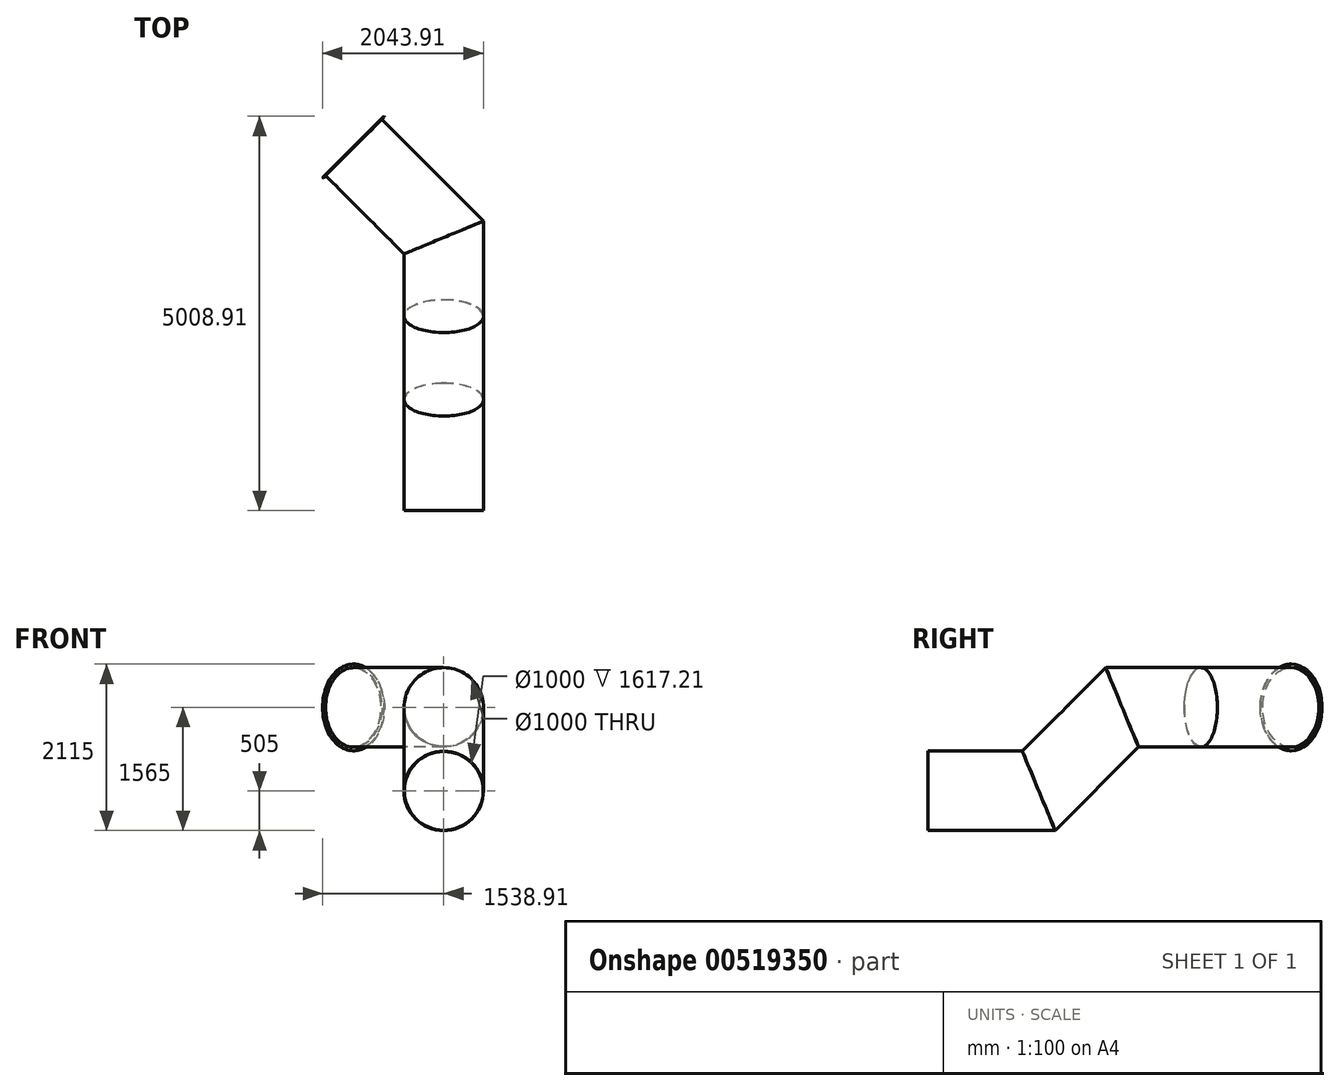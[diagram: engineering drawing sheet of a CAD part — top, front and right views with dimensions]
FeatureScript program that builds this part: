
annotation { "Feature Type Name" : "Feature", "Feature Type Description" : "" }
export const myFeature = defineFeature(function(context is Context, id is Id, definition is map)
    precondition{}
    {
        {
            var Q0;
            Q0=qCreatedBy(makeId("Top.planeOp"),FACE);
            var sketch = newSketch(context, id + "F0", { "sketchPlane" : qUnion([Q0])});
            skLineSegment(sketch, "E0", {"start": v(0, 0) * mm, "end": v(-1150, 1150) * mm});
            skLineSegment(sketch, "E1", {"start": v(0, 0) * mm, "end": v(0, -1000) * mm});
            skSolve(sketch);
        }
        {
            var Q0;
            Q0=qCreatedBy(makeId("Right.planeOp"),FACE);
            var sketch = newSketch(context, id + "F1", { "sketchPlane" : qUnion([Q0])});
            skPoint(sketch, "E2.0", {"position": v(-1000, 0) * mm});
            skLineSegment(sketch, "E3", {"start": v(-1000, 0) * mm, "end": v(-2060, -1060) * mm});
            skLineSegment(sketch, "E4", {"start": v(-2060, -1060) * mm, "end": v(-3470, -1060) * mm});
            skSolve(sketch);
        }
        {
            var Q0;
            Q0=qCreatedBy(makeId("Front.planeOp"),FACE);
            cPlane(context, id + "F2", {"entities" : qUnion([Q0]), "cplaneType" : CPlaneType.OFFSET, "offset" : 3470 * mm, "width" : 150 * mm, "height" : 150 * mm});
        }
        {
            var Q0;
            Q0=qCreatedBy(id+"F2.planeOp",FACE);
            var sketch = newSketch(context, id + "F3", { "sketchPlane" : qUnion([Q0])});
            skPoint(sketch, "E5.0", {"position": v(0, -1060) * mm});
            skCircle(sketch, "E6", {"center": v(0, -1060) * mm, "radius": 500 * mm});
            skCircle(sketch, "E7", {"center": v(0, -1060) * mm, "radius": 505 * mm});
            skSolve(sketch);
        }
        {
            var Q0;
            Q0 = qSketchRegion(id + "F3", true);
            var Q1;
            Q1 = qConstructionFilter(qBodyType(qCreatedBy(id + "F1" ,EDGE), BodyType.WIRE), ConstructionObject.NO);
            var Q2;
            Q2 = qConstructionFilter(qBodyType(qCreatedBy(id + "F0" ,EDGE), BodyType.WIRE), ConstructionObject.NO);
            sweep(context, id + "F4", {"profiles" : qUnion([Q0]), "path" : qUnion([Q1, Q2])});
        }
        {
            var Q0;
            Q0=makeQuery(id+"F4.opSweep","CAP_FACE",FACE,{"disambiguationData":[OSD([sQuery(id+"F0.wireOp",VERTEX,"E0.end"),sQuery(id+"F3.wireOp",EDGE,"E6"),sQuery(id+"F3.wireOp",EDGE,"E7")])],"isStart":false});
            var sketch = newSketch(context, id + "F5", { "sketchPlane" : qUnion([Q0])});
            skCircle(sketch, "E8.0", {"center": v(0, 0) * mm, "radius": 500 * mm});
            skCircle(sketch, "E9", {"center": v(0, 0) * mm, "radius": 550 * mm});
            skSolve(sketch);
        }
        {
            var Q0;
            Q0 = qSketchRegion(id + "F5", true);
            extrude(context, id + "F6", {"entities" : qUnion([Q0]), "operationType" : NewBodyOperationType.ADD, "oppositeDirection" : true, "depth" : 10 * mm, "offsetDistance" : 25 * mm});
        }
    });
